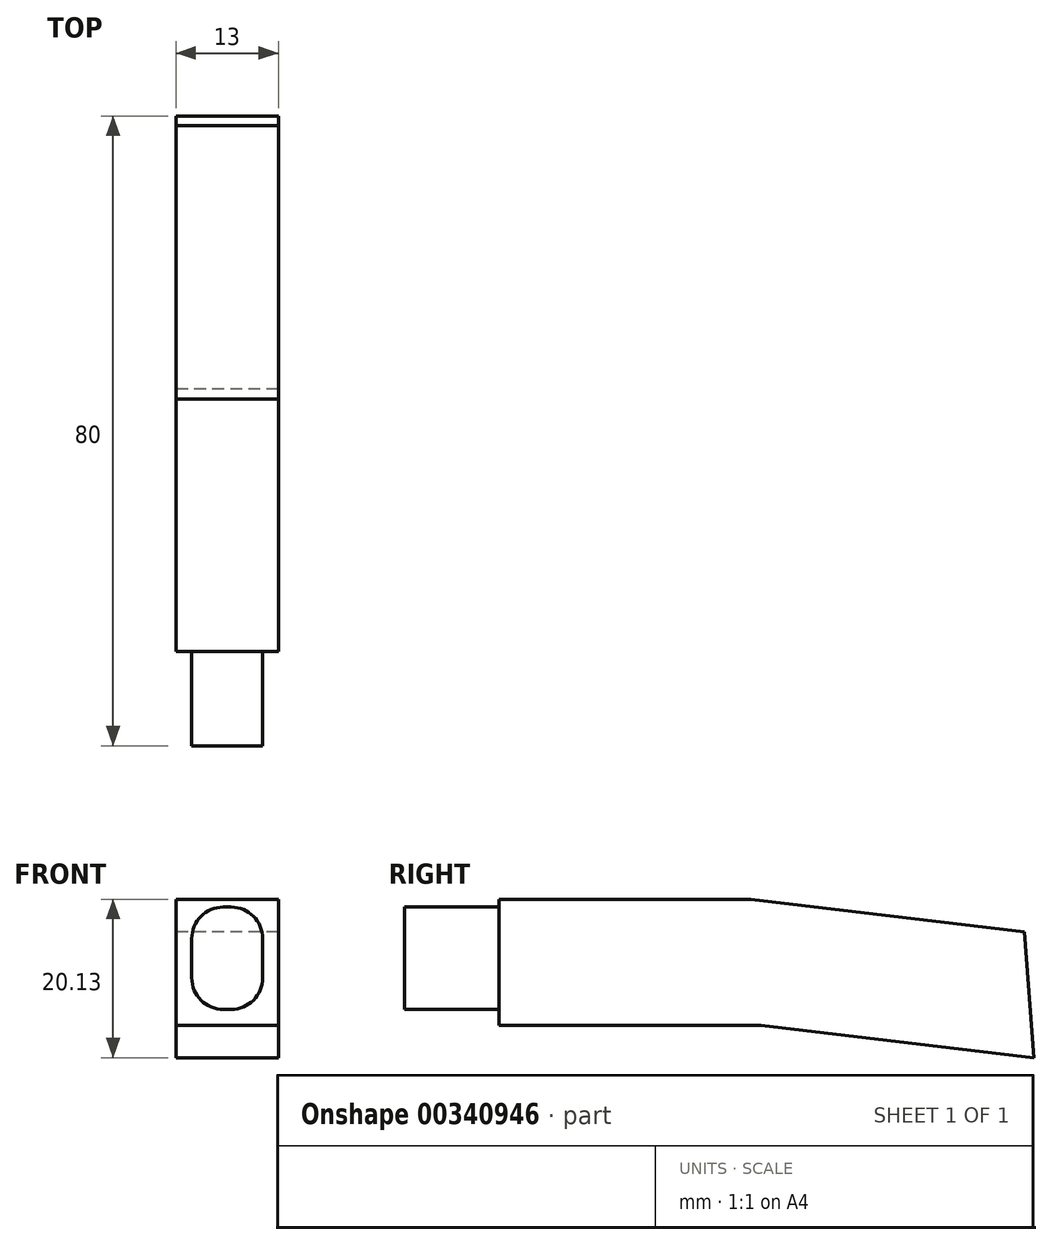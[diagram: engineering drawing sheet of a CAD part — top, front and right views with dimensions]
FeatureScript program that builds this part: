
annotation { "Feature Type Name" : "Feature", "Feature Type Description" : "" }
export const myFeature = defineFeature(function(context is Context, id is Id, definition is map)
    precondition{}
    {
        {
            var Q0;
            Q0=qCreatedBy(makeId("Right.planeOp"),FACE);
            var sketch = newSketch(context, id + "F0", { "sketchPlane" : qUnion([Q0])});
            skLineSegment(sketch, "E0.bottom", {"start": v(-38.76, 8) * mm, "end": v(5.29, 8) * mm});
            skLineSegment(sketch, "E0.top", {"start": v(-38.76, -8) * mm, "end": v(6.53, -8) * mm});
            skLineSegment(sketch, "E0.left", {"start": v(-38.76, 8) * mm, "end": v(-38.76, -8) * mm});
            skLineSegment(sketch, "E1", {"start": v(6.53, -8) * mm, "end": v(41.24, -12.13) * mm});
            skLineSegment(sketch, "E2", {"start": v(40, 3.87) * mm, "end": v(5.29, 8) * mm});
            skLineSegment(sketch, "E3", {"start": v(40, 3.87) * mm, "end": v(41.24, -12.13) * mm});
            skSolve(sketch);
        }
        {
            var Q0;
            Q0 = qSketchRegion(id + "F0", true);
            extrude(context, id + "F1", {"entities" : qUnion([Q0]), "endBound" : BoundingType.SYMMETRIC, "depth" : 13 * mm});
        }
        {
            var Q0;
            Q0=makeQuery(id+"F1.opExtrude","SWEPT_FACE",FACE,{"disambiguationData":[OSD([sQuery(id+"F0.wireOp",EDGE,"E0.left")])]});
            var sketch = newSketch(context, id + "F2", { "sketchPlane" : qUnion([Q0])});
            skLineSegment(sketch, "E4.bottom", {"start": v(-4.5, 7) * mm, "end": v(4.5, 7) * mm});
            skLineSegment(sketch, "E4.top", {"start": v(-4.5, -6) * mm, "end": v(4.5, -6) * mm});
            skLineSegment(sketch, "E4.left", {"start": v(-4.5, 7) * mm, "end": v(-4.5, -6) * mm});
            skLineSegment(sketch, "E4.right", {"start": v(4.5, 7) * mm, "end": v(4.5, -6) * mm});
            skSolve(sketch);
        }
        {
            var Q0;
            Q0=makeQuery(id+"F2.imprint","IMPRINT",FACE,{"disambiguationData":[TD([[makeQuery(id+"F2.imprint","IMPRINT",EDGE,{"derivedFrom":sQuery(id+"F2.wireOp",EDGE,"E4.bottom")}),1.0]])]});
            extrude(context, id + "F3", {"entities" : qUnion([Q0]), "operationType" : NewBodyOperationType.REMOVE, "oppositeDirection" : true, "depth" : 12 * mm});
        }
        {
            var Q0;
            Q0=makeQuery(id+"F3.boolean.opBoolean","COPY",EDGE,{"derivedFrom":makeQuery(id+"F3.opExtrude","SWEPT_EDGE",EDGE,{"disambiguationData":[OSD([sQuery(id+"F2.wireOp",EDGE,"E4.bottom"),sQuery(id+"F2.wireOp",EDGE,"E4.right")])]})});
            var Q1;
            Q1=makeQuery(id+"F3.boolean.opBoolean","COPY",EDGE,{"derivedFrom":makeQuery(id+"F3.opExtrude","SWEPT_EDGE",EDGE,{"disambiguationData":[OSD([sQuery(id+"F2.wireOp",EDGE,"E4.bottom"),sQuery(id+"F2.wireOp",EDGE,"E4.left")])]})});
            var Q2;
            Q2=makeQuery(id+"F3.boolean.opBoolean","COPY",EDGE,{"derivedFrom":makeQuery(id+"F3.opExtrude","SWEPT_EDGE",EDGE,{"disambiguationData":[OSD([sQuery(id+"F2.wireOp",EDGE,"E4.top"),sQuery(id+"F2.wireOp",EDGE,"E4.right")])]})});
            var Q3;
            Q3=makeQuery(id+"F3.boolean.opBoolean","COPY",EDGE,{"derivedFrom":makeQuery(id+"F3.opExtrude","SWEPT_EDGE",EDGE,{"disambiguationData":[OSD([sQuery(id+"F2.wireOp",EDGE,"E4.top"),sQuery(id+"F2.wireOp",EDGE,"E4.left")])]})});
            fillet(context, id + "F4", {"entities" : qUnion([Q0, Q1, Q2, Q3]), "radius" : 4 * mm, "tangentPropagation" : true, "allowEdgeOverflow" : false});
        }
        {
            var Q0;
            Q0=makeQuery(id+"F3.boolean.opBoolean","COPY",FACE,{"derivedFrom":makeQuery(id+"F3.opExtrude","CAP_FACE",FACE,{"disambiguationData":[OSD([sQuery(id+"F0.wireOp",EDGE,"E0.bottom"),sQuery(id+"F0.wireOp",EDGE,"E0.top"),sQuery(id+"F0.wireOp",EDGE,"E0.left"),sQuery(id+"F2.wireOp",EDGE,"E4.bottom"),sQuery(id+"F2.wireOp",EDGE,"E4.top"),sQuery(id+"F2.wireOp",EDGE,"E4.left"),sQuery(id+"F2.wireOp",EDGE,"E4.right")])],"isStart":false})});
            var sketch = newSketch(context, id + "F5", { "sketchPlane" : qUnion([Q0])});
            skArc(sketch, "E5", {"start": v(29, -21) * mm, "mid": v(1.45, 7.96) * mm, "end": v(-28.86, -18.11) * mm});
            skLineSegment(sketch, "E6", {"start": v(29, -21) * mm, "end": v(29, 12.29) * mm});
            skLineSegment(sketch, "E7", {"start": v(29, 12.29) * mm, "end": v(-28.57, 12.29) * mm});
            skLineSegment(sketch, "E8", {"start": v(-28.57, 12.29) * mm, "end": v(-28.86, -18.11) * mm});
            skLineSegment(sketch, "E9", {"start": v(14.33, -4.21) * mm, "end": v(19.08, -18.66) * mm});
            skLineSegment(sketch, "E10", {"start": v(19.08, -18.66) * mm, "end": v(-17.4, -18.66) * mm});
            skLineSegment(sketch, "E11", {"start": v(-17.4, -18.66) * mm, "end": v(-11, -5.83) * mm});
            skArc(sketch, "E12.trimOffspring", {"start": v(-11, -5.83) * mm, "mid": v(1.85, -7.94) * mm, "end": v(14.33, -4.21) * mm});
            skSolve(sketch);
        }
        {
            var Q0;
            {var subQ0=sQuery(id+"F5.wireOp",EDGE,"E5");var subQ1=sQuery(id+"F0.wireOp",EDGE,"E0.left");var subQ2=makeQuery(id+"F3.boolean.opBoolean","COPY",EDGE,{"derivedFrom":makeQuery(id+"F3.opExtrude","CAP_EDGE",EDGE,{"disambiguationData":[OSD([subQ1]),TDD([makeQuery(id+"F2.imprint","IMPRINT",EDGE,{"derivedFrom":makeQuery(id+"F1.opExtrude","CAP_EDGE",EDGE,{"disambiguationData":[OSD([subQ1])],"isStart":false})})])],"isStart":false})});var subQ3=makeQuery(id+"F5.imprint","INTERSECT",VERTEX,{"derivedFrom":[subQ2,subQ0]});Q0=makeQuery(id+"F5.imprint","IMPRINT",FACE,{"disambiguationData":[TD([[makeQuery(id+"F5.imprint","IMPRINT",EDGE,{"disambiguationData":[TD([[subQ3,-1.0]])],"derivedFrom":subQ0}),-1.0]])]});}
            var Q1;
            {var subQ0=sQuery(id+"F5.wireOp",EDGE,"E5");var subQ1=sQuery(id+"F0.wireOp",EDGE,"E0.left");var subQ2=makeQuery(id+"F3.boolean.opBoolean","COPY",EDGE,{"derivedFrom":makeQuery(id+"F3.opExtrude","CAP_EDGE",EDGE,{"disambiguationData":[OSD([subQ1]),TDD([makeQuery(id+"F2.imprint","IMPRINT",EDGE,{"derivedFrom":makeQuery(id+"F1.opExtrude","CAP_EDGE",EDGE,{"disambiguationData":[OSD([subQ1])],"isStart":true})})])],"isStart":false})});var subQ3=makeQuery(id+"F5.imprint","INTERSECT",VERTEX,{"derivedFrom":[subQ2,subQ0]});Q1=makeQuery(id+"F5.imprint","IMPRINT",FACE,{"disambiguationData":[TD([[makeQuery(id+"F5.imprint","IMPRINT",EDGE,{"disambiguationData":[TD([[subQ3,1.0]])],"derivedFrom":subQ0}),-1.0]])]});}
            var Q2;
            {var subQ0=sQuery(id+"F5.wireOp",EDGE,"E12.trimOffspring");var subQ1=sQuery(id+"F0.wireOp",EDGE,"E0.left");var subQ2=makeQuery(id+"F3.boolean.opBoolean","COPY",EDGE,{"derivedFrom":makeQuery(id+"F3.opExtrude","CAP_EDGE",EDGE,{"disambiguationData":[OSD([subQ1]),TDD([makeQuery(id+"F2.imprint","IMPRINT",EDGE,{"derivedFrom":makeQuery(id+"F1.opExtrude","CAP_EDGE",EDGE,{"disambiguationData":[OSD([subQ1])],"isStart":false})})])],"isStart":false})});var subQ3=makeQuery(id+"F5.imprint","INTERSECT",VERTEX,{"derivedFrom":[subQ2,subQ0]});Q2=makeQuery(id+"F5.imprint","IMPRINT",FACE,{"disambiguationData":[TD([[makeQuery(id+"F5.imprint","IMPRINT",EDGE,{"disambiguationData":[TD([[subQ3,1.0]])],"derivedFrom":subQ0}),-1.0]])]});}
            var Q3;
            {var subQ0=sQuery(id+"F5.wireOp",EDGE,"E12.trimOffspring");var subQ1=sQuery(id+"F0.wireOp",EDGE,"E0.left");var subQ2=makeQuery(id+"F3.boolean.opBoolean","COPY",EDGE,{"derivedFrom":makeQuery(id+"F3.opExtrude","CAP_EDGE",EDGE,{"disambiguationData":[OSD([subQ1]),TDD([makeQuery(id+"F2.imprint","IMPRINT",EDGE,{"derivedFrom":makeQuery(id+"F1.opExtrude","CAP_EDGE",EDGE,{"disambiguationData":[OSD([subQ1])],"isStart":true})})])],"isStart":false})});var subQ3=makeQuery(id+"F5.imprint","INTERSECT",VERTEX,{"derivedFrom":[subQ2,subQ0]});Q3=makeQuery(id+"F5.imprint","IMPRINT",FACE,{"disambiguationData":[TD([[makeQuery(id+"F5.imprint","IMPRINT",EDGE,{"disambiguationData":[TD([[subQ3,-1.0]])],"derivedFrom":subQ0}),-1.0]])]});}
            extrude(context, id + "F6", {"entities" : qUnion([Q0, Q1, Q2, Q3]), "operationType" : NewBodyOperationType.REMOVE, "oppositeDirection" : true, "depth" : 33 * mm});
        }
        {
            var Q0;
            Q0=makeQuery(id+"F1.opExtrude","CAP_FACE",FACE,{"disambiguationData":[OSD([sQuery(id+"F0.wireOp",EDGE,"E0.bottom"),sQuery(id+"F0.wireOp",EDGE,"E0.top"),sQuery(id+"F0.wireOp",EDGE,"E0.left"),sQuery(id+"F0.wireOp",EDGE,"E1"),sQuery(id+"F0.wireOp",EDGE,"E2"),sQuery(id+"F0.wireOp",EDGE,"E3")])],"isStart":true});
            var sketch = newSketch(context, id + "F7", { "sketchPlane" : qUnion([Q0])});
            skLineSegment(sketch, "E13", {"start": v(-40, 3.87) * mm, "end": v(-38.14, -11.76) * mm});
            skSolve(sketch);
        }
        {
            var Q0;
            Q0=qCreatedBy(makeId("Front.planeOp"),FACE);
            var Q1;
            Q1=sQuery(id+"F7.wireOp",EDGE,"E13");
            cPlane(context, id + "F8", {"entities" : qUnion([Q0, Q1]), "cplaneType" : CPlaneType.LINE_ANGLE, "offset" : 25 * mm, "angle" : 0 * degree, "width" : 150 * mm, "height" : 150 * mm});
        }
    });
